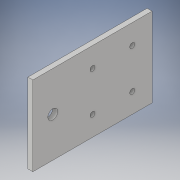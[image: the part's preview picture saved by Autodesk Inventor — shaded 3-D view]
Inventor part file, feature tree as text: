
AUTODESK INVENTOR PART (.ipt)
format: ipt  version: 2017 (Build 210142000, 142)  size: 107,520 bytes
history: native  units: in
note: dims shown in document units (in); Inventor stores cm internally (conversion verified against a paired STEP export)
features: extrude x1, sketch x1
ambient origin geometry x8: Origin, YZ Plane, XZ Plane, XY Plane, X Axis, Y Axis, Z Axis, Center Point
bodies: Solid1 (feature_tree)
feature tree (2):
  extrude  "Extrusion1"  Depth=3.0in
  sketch  "Sketch1"  dims[d0=2.0in d1=3.0in d2=2.0in d3=0.5in d4=0.5in d5=0.5in d6=0.125in d7=0.125in d8=0.5in d9=0.25in d10=0.125in d11=0.0in]
